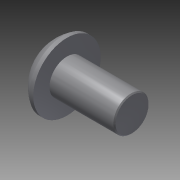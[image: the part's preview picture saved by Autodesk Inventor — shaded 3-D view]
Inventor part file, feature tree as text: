
AUTODESK INVENTOR PART (.ipt)
format: ipt  version: 2015 (Build 190159000, 159)  size: 144,384 bytes
history: native  units: in
note: dims shown in document units (in); Inventor stores cm internally (conversion verified against a paired STEP export)
features: other x3, extrude x1, chamfer x1, imported_body x1, sketch x1
ambient origin geometry x8: Origin, YZ Plane, XZ Plane, XY Plane, X Axis, Y Axis, Z Axis, Center Point
bodies: Body1 (feature_tree)
feature tree (7):
  other  "Motor Bolt 0.25 inch"
  parser-record x1  (decoder bookkeeping rows leaked as tree rows — omitted from the tree; the rows remain in map.json)
  other  "Motor Bolt"
  extrude  "thread length"  Depth=0.25in TaperAngle=0.0deg
  chamfer  "thread chamfer"  Distance=0.004in Angle=45.0deg
  imported_body  "Base1"
  sketch  "Sketch1"  dims[d0=0.135in d1=0.25in d2=0.0in d3=0.004in d4=0.125in d5=45.0deg d7=0.0in d8=0.0in]
